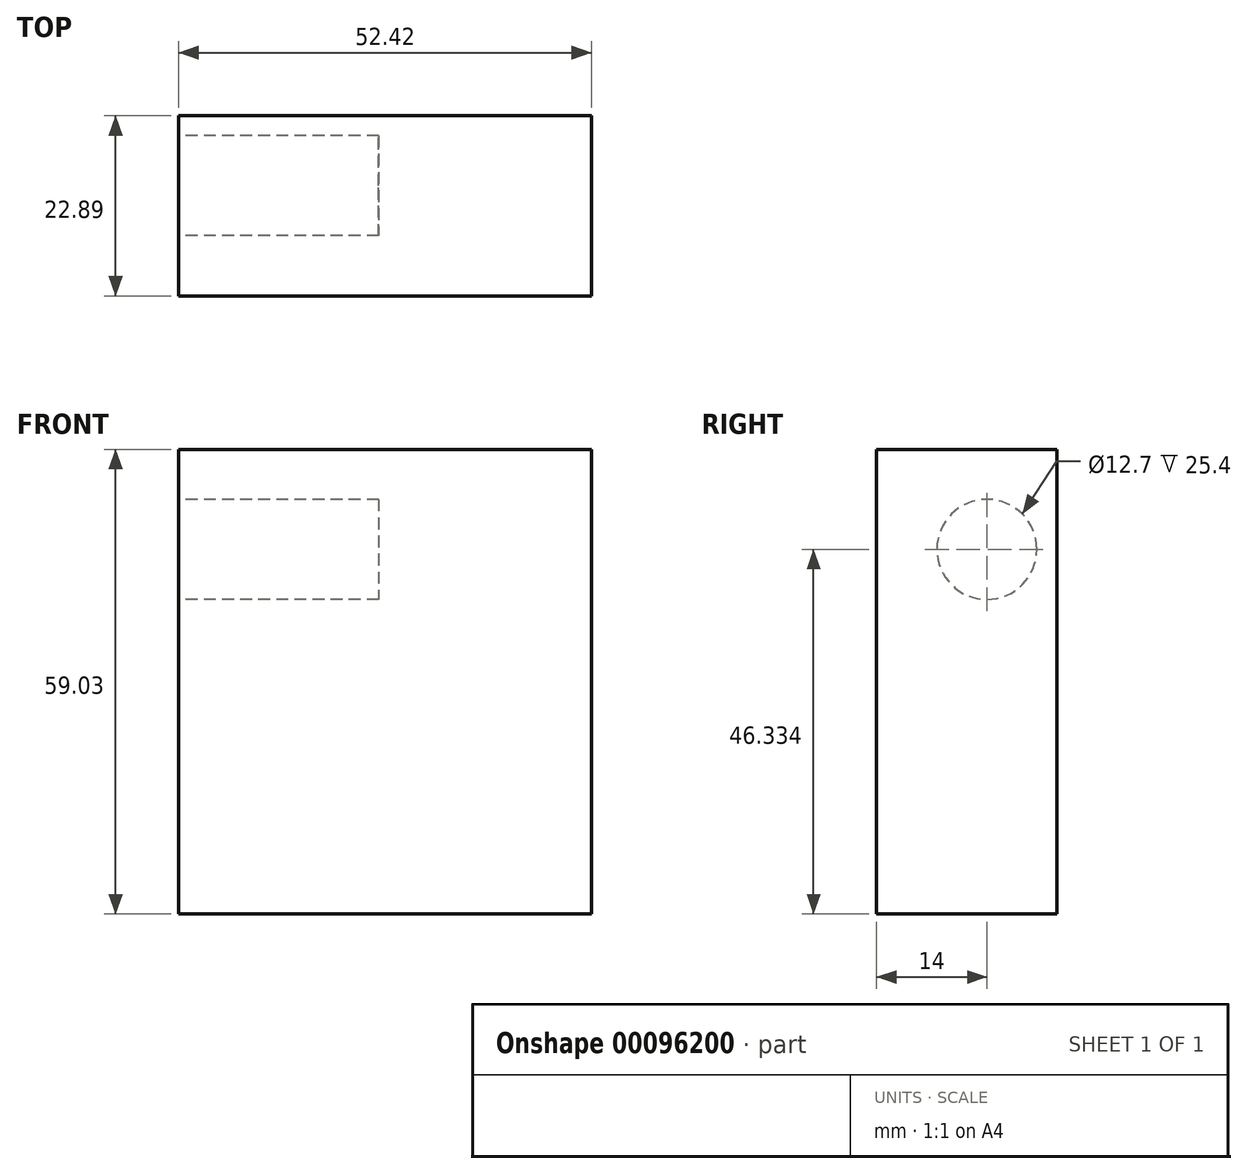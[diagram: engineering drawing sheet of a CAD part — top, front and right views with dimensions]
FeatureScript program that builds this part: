
annotation { "Feature Type Name" : "Feature", "Feature Type Description" : "" }
export const myFeature = defineFeature(function(context is Context, id is Id, definition is map)
    precondition{}
    {
        {
            var Q0;
            Q0=qCreatedBy(makeId("Top.planeOp"),FACE);
            var sketch = newSketch(context, id + "F0", { "sketchPlane" : qUnion([Q0])});
            skLineSegment(sketch, "E0.bottom", {"start": v(-62.06, 43.53) * mm, "end": v(-9.64, 43.53) * mm});
            skLineSegment(sketch, "E0.top", {"start": v(-62.06, 20.64) * mm, "end": v(-9.64, 20.64) * mm});
            skLineSegment(sketch, "E0.left", {"start": v(-62.06, 43.53) * mm, "end": v(-62.06, 20.64) * mm});
            skLineSegment(sketch, "E0.right", {"start": v(-9.64, 43.53) * mm, "end": v(-9.64, 20.64) * mm});
            skSolve(sketch);
        }
        {
            var Q0;
            Q0=makeQuery(id+"F0.imprint","IMPRINT",FACE,{"disambiguationData":[TD([[makeQuery(id+"F0.imprint","IMPRINT",EDGE,{"derivedFrom":sQuery(id+"F0.wireOp",EDGE,"E0.bottom")}),-1.0]])]});
            extrude(context, id + "F1", {"entities" : qUnion([Q0]), "depth" : 59.03 * mm});
        }
        {
            var Q0;
            Q0=makeQuery(id+"F1.opExtrude","SWEPT_FACE",FACE,{"disambiguationData":[OSD([sQuery(id+"F0.wireOp",EDGE,"E0.left")])]});
            var sketch = newSketch(context, id + "F2", { "sketchPlane" : qUnion([Q0])});
            skCircle(sketch, "E1", {"center": v(-34.64, 46.33) * mm, "radius": 6.35 * mm});
            skSolve(sketch);
        }
        {
            var Q0;
            Q0 = qSketchRegion(id + "F2", true);
            extrude(context, id + "F3", {"entities" : qUnion([Q0]), "operationType" : NewBodyOperationType.REMOVE, "oppositeDirection" : true, "depth" : 25.4 * mm});
        }
    });
